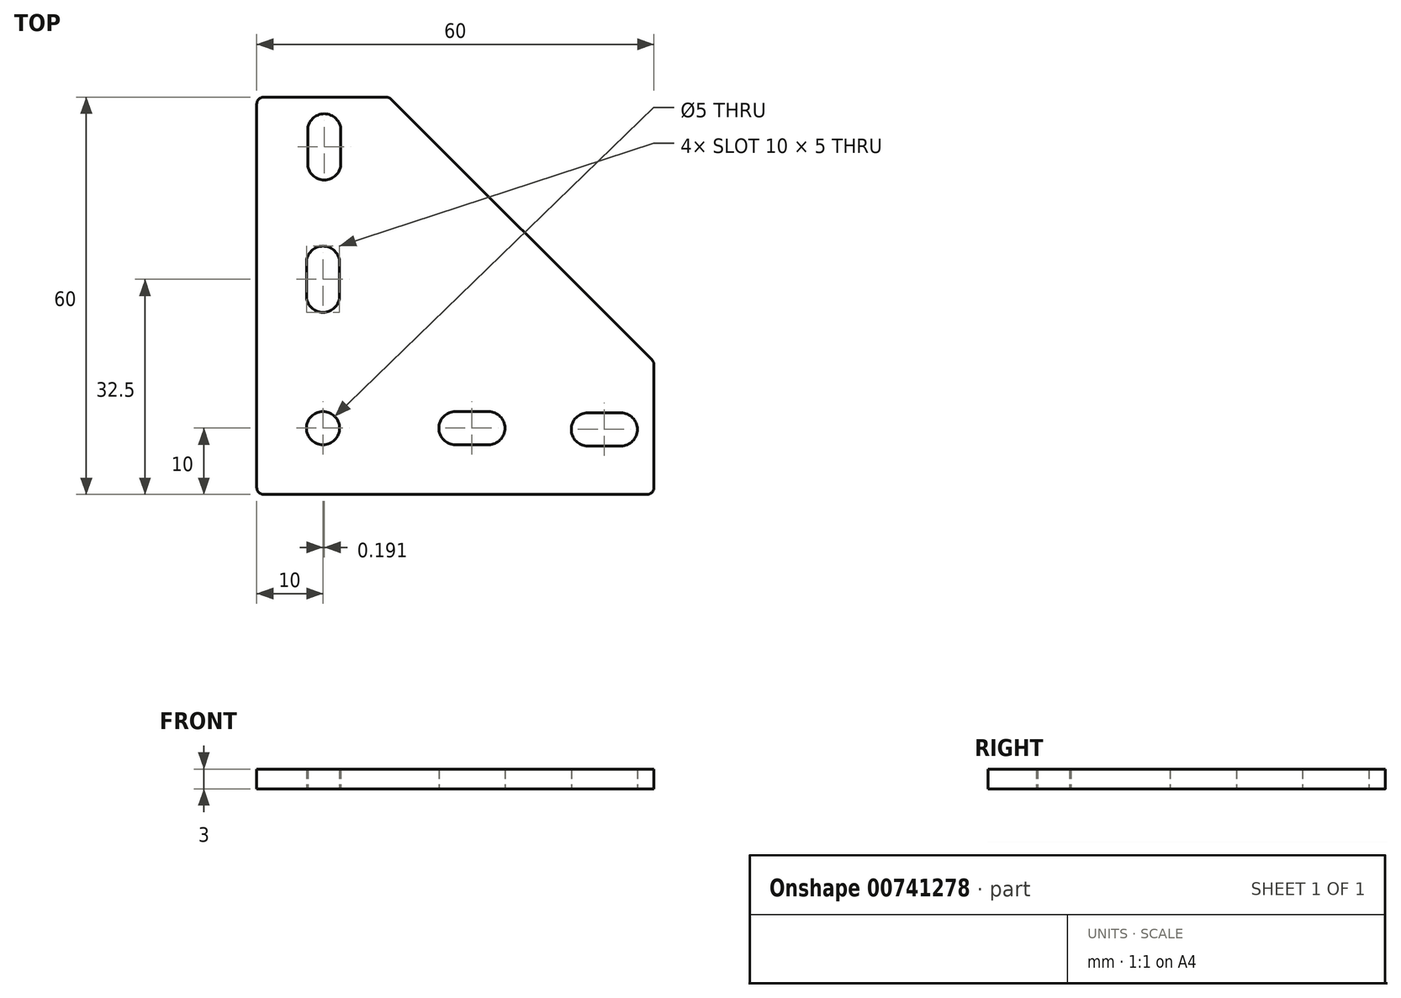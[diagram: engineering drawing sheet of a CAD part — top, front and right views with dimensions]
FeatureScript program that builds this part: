
annotation { "Feature Type Name" : "Feature", "Feature Type Description" : "" }
export const myFeature = defineFeature(function(context is Context, id is Id, definition is map)
    precondition{}
    {
        {
            var Q0;
            Q0=qCreatedBy(makeId("Top.planeOp"),FACE);
            var sketch = newSketch(context, id + "F0", { "sketchPlane" : qUnion([Q0])});
            skLineSegment(sketch, "E0", {"start": v(0, 1) * mm, "end": v(0, 59) * mm});
            skLineSegment(sketch, "E1", {"start": v(1, 60) * mm, "end": v(19.59, 60) * mm});
            skLineSegment(sketch, "E2", {"start": v(20.3, 59.7) * mm, "end": v(59.7, 20.3) * mm});
            skLineSegment(sketch, "E3", {"start": v(60, 19.59) * mm, "end": v(60, 1) * mm});
            skLineSegment(sketch, "E4", {"start": v(59, 0) * mm, "end": v(1, 0) * mm});
            skLineSegment(sketch, "E5", {"start": v(0, 20) * mm, "end": v(20, 20) * mm, "construction": true});
            skLineSegment(sketch, "E6", {"start": v(20, 20) * mm, "end": v(20, 0) * mm, "construction": true});
            skLineSegment(sketch, "E7", {"start": v(60, 10) * mm, "end": v(20, 10) * mm, "construction": true});
            skLineSegment(sketch, "E8", {"start": v(10, 20) * mm, "end": v(10, 60) * mm, "construction": true});
            skArc(sketch, "E9", {"start": v(30, 12.5) * mm, "mid": v(27.5, 10) * mm, "end": v(30, 7.5) * mm});
            skPoint(sketch, "E9.centerSnap0", {"position": v(30, 0) * mm});
            skArc(sketch, "E10", {"start": v(35, 7.5) * mm, "mid": v(37.5, 10) * mm, "end": v(35, 12.5) * mm});
            skLineSegment(sketch, "E11", {"start": v(30, 12.5) * mm, "end": v(35, 12.5) * mm});
            skLineSegment(sketch, "E12", {"start": v(30, 7.5) * mm, "end": v(35, 7.5) * mm});
            skLineSegment(sketch, "E13", {"start": v(10, 20) * mm, "end": v(10, 10) * mm, "construction": true});
            skLineSegment(sketch, "E14", {"start": v(10, 10) * mm, "end": v(20, 10) * mm, "construction": true});
            skArc(sketch, "E15", {"start": v(50, 12.3) * mm, "mid": v(47.5, 9.8) * mm, "end": v(50, 7.3) * mm});
            skArc(sketch, "E16", {"start": v(55, 7.3) * mm, "mid": v(57.5, 9.8) * mm, "end": v(55, 12.3) * mm});
            skLineSegment(sketch, "E17", {"start": v(50, 12.3) * mm, "end": v(55, 12.3) * mm});
            skLineSegment(sketch, "E18", {"start": v(50, 7.3) * mm, "end": v(55, 7.3) * mm});
            skArc(sketch, "E19.1.0", {"start": v(7.7, 50) * mm, "mid": v(10.2, 47.5) * mm, "end": v(12.7, 50) * mm});
            skLineSegment(sketch, "E19.1.1", {"start": v(7.7, 50) * mm, "end": v(7.7, 55) * mm});
            skArc(sketch, "E19.1.2", {"start": v(7.5, 30) * mm, "mid": v(10, 27.5) * mm, "end": v(12.5, 30) * mm});
            skArc(sketch, "E19.1.3", {"start": v(12.5, 35) * mm, "mid": v(10, 37.5) * mm, "end": v(7.5, 35) * mm});
            skLineSegment(sketch, "E19.1.4", {"start": v(7.5, 30) * mm, "end": v(7.5, 35) * mm});
            skLineSegment(sketch, "E19.1.5", {"start": v(12.5, 30) * mm, "end": v(12.5, 35) * mm});
            skLineSegment(sketch, "E19.1.6", {"start": v(12.7, 50) * mm, "end": v(12.7, 55) * mm});
            skArc(sketch, "E19.1.7", {"start": v(12.7, 55) * mm, "mid": v(10.2, 57.5) * mm, "end": v(7.7, 55) * mm});
            skPoint(sketch, "E19.center", {"position": v(10, 10) * mm});
            skLineSegment(sketch, "E19.anchor1", {"start": v(10, 10) * mm, "end": v(30, 10) * mm, "construction": true});
            skLineSegment(sketch, "E19.anchor2", {"start": v(10, 10) * mm, "end": v(10, 30) * mm, "construction": true});
            skCircle(sketch, "E20", {"center": v(10, 10) * mm, "radius": 2.5 * mm});
            skPoint(sketch, "E21.visualSharp", {"position": v(0, 60) * mm});
            skArc(sketch, "E21.filletArc", {"start": v(1, 60) * mm, "mid": v(0.3, 59.7) * mm, "end": v(0, 59) * mm});
            skPoint(sketch, "E22.visualSharp", {"position": v(20, 60) * mm});
            skArc(sketch, "E22.filletArc", {"start": v(20.3, 59.7) * mm, "mid": v(19.97, 59.92) * mm, "end": v(19.59, 60) * mm});
            skPoint(sketch, "E23.visualSharp", {"position": v(60, 20) * mm});
            skArc(sketch, "E23.filletArc", {"start": v(60, 19.59) * mm, "mid": v(59.92, 19.97) * mm, "end": v(59.7, 20.3) * mm});
            skPoint(sketch, "E24.visualSharp", {"position": v(60, 0) * mm});
            skArc(sketch, "E24.filletArc", {"start": v(59, 0) * mm, "mid": v(59.7, 0.3) * mm, "end": v(60, 1) * mm});
            skPoint(sketch, "E25.visualSharp", {"position": v(0, 0) * mm});
            skArc(sketch, "E25.filletArc", {"start": v(0, 1) * mm, "mid": v(0.3, 0.3) * mm, "end": v(1, 0) * mm});
            skSolve(sketch);
        }
        {
            var Q0;
            Q0 = qSketchRegion(id + "F0", true);
            extrude(context, id + "F1", {"entities" : qUnion([Q0]), "depth" : 3 * mm, "offsetDistance" : 25 * mm});
        }
    });
